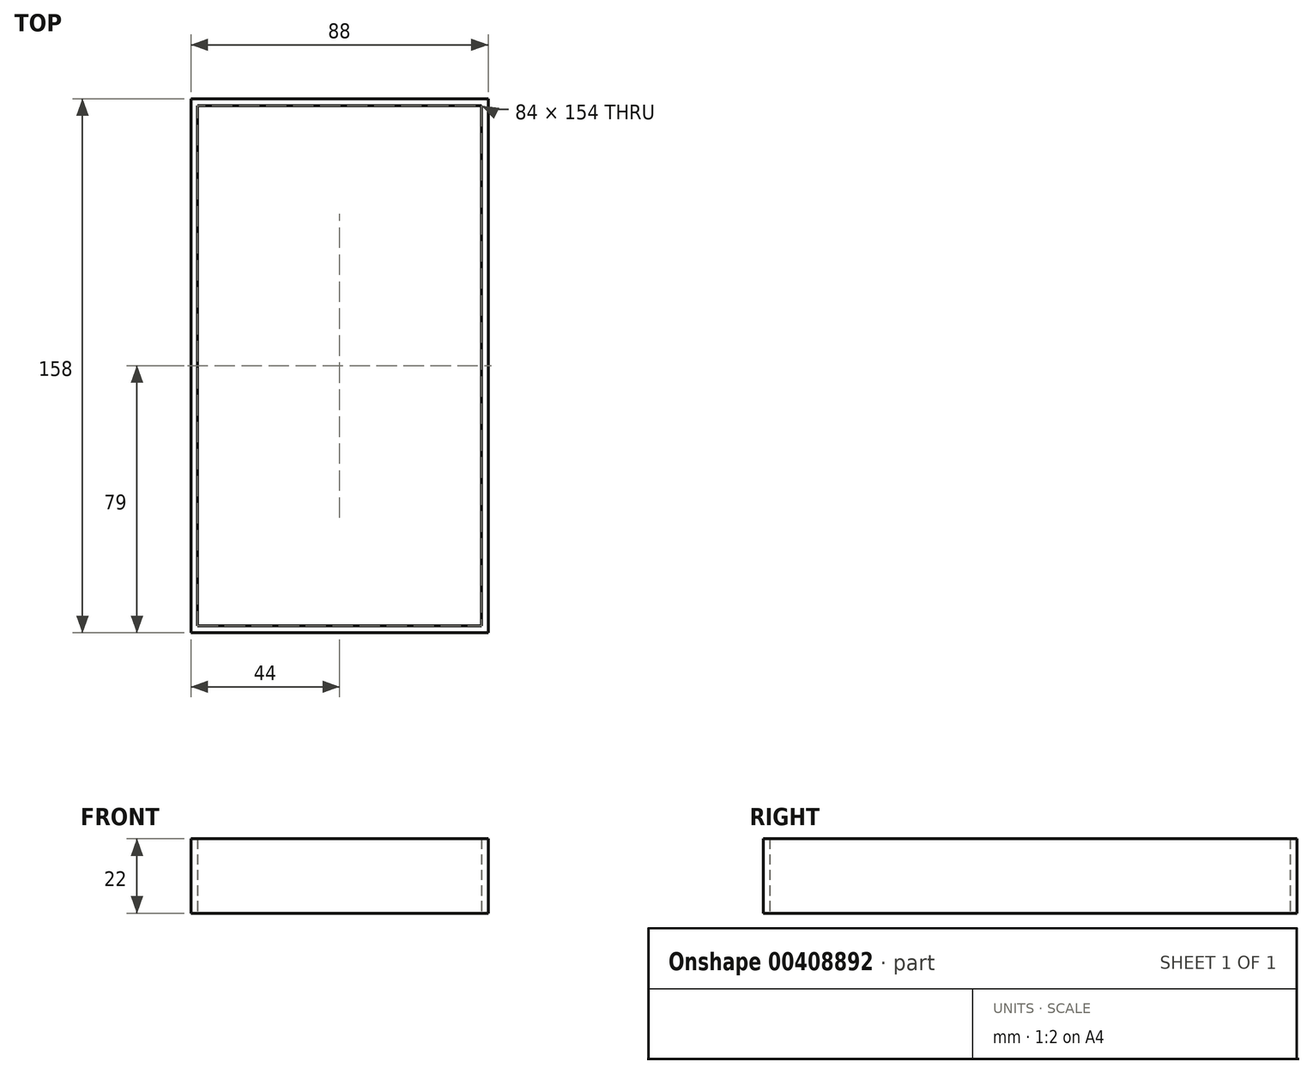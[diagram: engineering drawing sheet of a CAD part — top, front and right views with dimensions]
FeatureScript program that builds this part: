
annotation { "Feature Type Name" : "Feature", "Feature Type Description" : "" }
export const myFeature = defineFeature(function(context is Context, id is Id, definition is map)
    precondition{}
    {
        {
            var Q0;
            Q0=qCreatedBy(makeId("Top.planeOp"),FACE);
            var sketch = newSketch(context, id + "F0", { "sketchPlane" : qUnion([Q0])});
            skLineSegment(sketch, "E0.bottom", {"start": v(44, -79) * mm, "end": v(-44, -79) * mm});
            skLineSegment(sketch, "E0.top", {"start": v(44, 79) * mm, "end": v(-44, 79) * mm});
            skLineSegment(sketch, "E0.left", {"start": v(44, -79) * mm, "end": v(44, 79) * mm});
            skLineSegment(sketch, "E0.right", {"start": v(-44, -79) * mm, "end": v(-44, 79) * mm});
            skPoint(sketch, "E0.middle", {"position": v(0, 0) * mm});
            skLineSegment(sketch, "E1.left", {"start": v(-44, -79) * mm, "end": v(-44, 81) * mm});
            skSolve(sketch);
        }
        {
            var Q0;
            Q0=makeQuery(id+"F0.imprint","IMPRINT",FACE,{"disambiguationData":[TD([[makeQuery(id+"F0.imprint","IMPRINT",EDGE,{"derivedFrom":sQuery(id+"F0.wireOp",EDGE,"E0.bottom")}),-1.0]])]});
            extrude(context, id + "F1", {"entities" : qUnion([Q0]), "depth" : 22 * mm});
        }
        {
            var Q0;
            Q0=makeQuery(id+"F1.opExtrude","CAP_FACE",FACE,{"disambiguationData":[OSD([sQuery(id+"F0.wireOp",EDGE,"E0.bottom"),sQuery(id+"F0.wireOp",EDGE,"E0.top"),sQuery(id+"F0.wireOp",EDGE,"E0.left"),sQuery(id+"F0.wireOp",EDGE,"E0.right")])],"isStart":false});
            var Q1;
            Q1=makeQuery(id+"F1.opExtrude","CAP_FACE",FACE,{"disambiguationData":[OSD([sQuery(id+"F0.wireOp",EDGE,"E0.bottom"),sQuery(id+"F0.wireOp",EDGE,"E0.top"),sQuery(id+"F0.wireOp",EDGE,"E0.left"),sQuery(id+"F0.wireOp",EDGE,"E1.right")])],"isStart":true});
            shell(context, id + "F2", {"entities" : qUnion([Q0, Q1]), "thickness" : 2 * mm});
        }
    });
